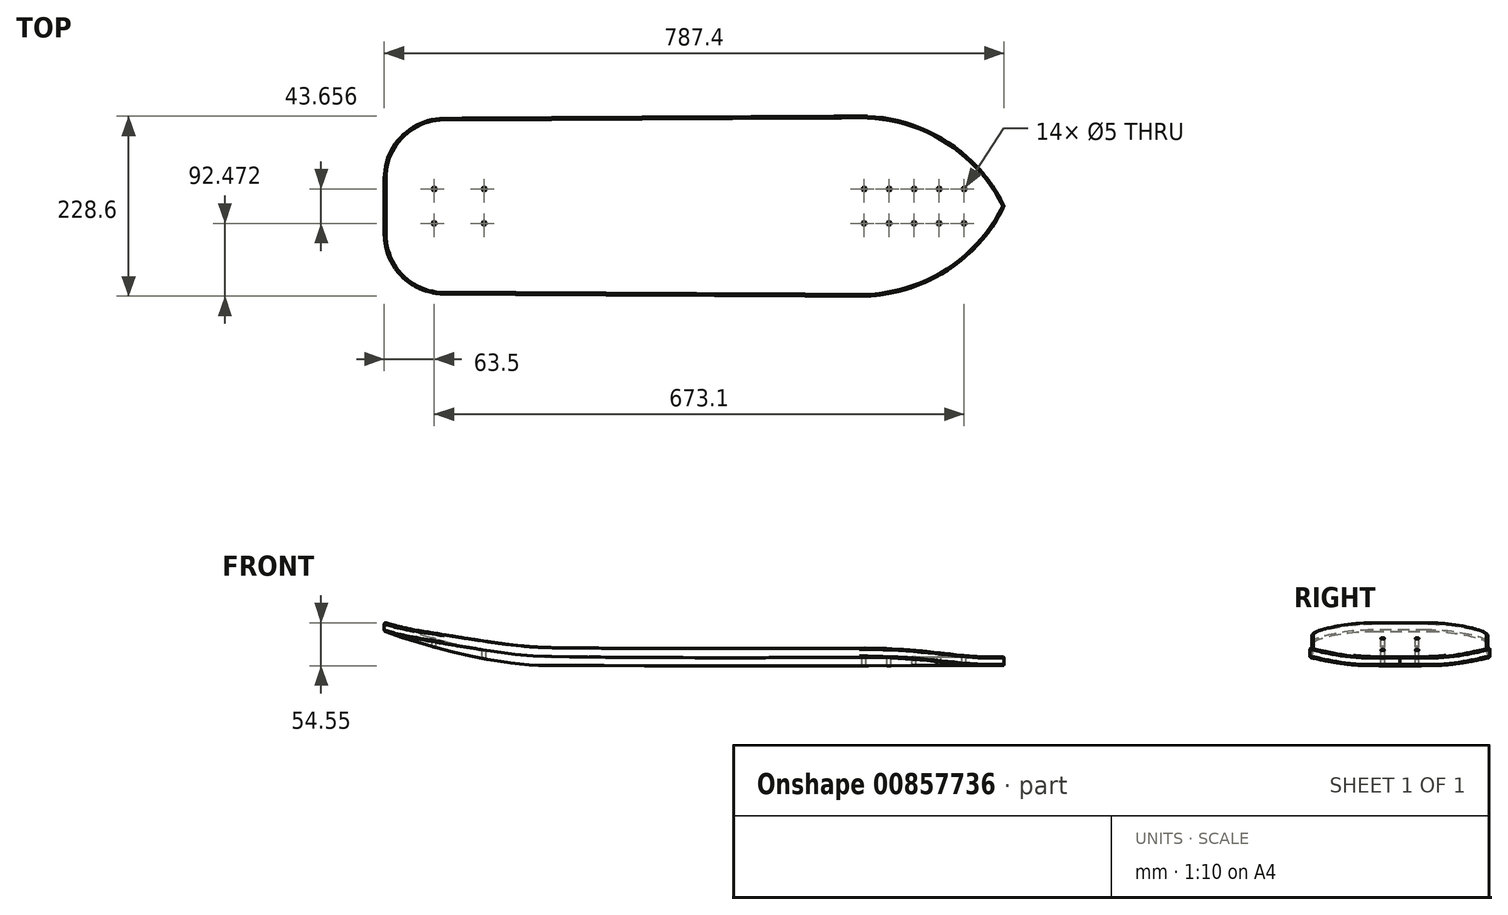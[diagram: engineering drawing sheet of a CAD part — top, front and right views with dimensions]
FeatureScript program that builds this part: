
annotation { "Feature Type Name" : "Feature", "Feature Type Description" : "" }
export const myFeature = defineFeature(function(context is Context, id is Id, definition is map)
    precondition{}
    {
        {
            var Q0;
            Q0=qCreatedBy(makeId("Front.planeOp"),FACE);
            var sketch = newSketch(context, id + "F0", { "sketchPlane" : qUnion([Q0])});
            skArc(sketch, "E0", {"start": v(-79.4, 6.95) * mm, "mid": v(-39.85, 1.74) * mm, "end": v(0, 0) * mm});
            skLineSegment(sketch, "E1", {"start": v(0, 0) * mm, "end": v(571.5, 0) * mm});
            skLineSegment(sketch, "E2", {"start": v(-79.4, 6.95) * mm, "end": v(-218.1, 31.4) * mm, "construction": true});
            skArc(sketch, "E3", {"start": v(-215.9, 43.91) * mm, "mid": v(-148.48, 22.36) * mm, "end": v(-79.4, 6.95) * mm});
            skLineSegment(sketch, "E4", {"start": v(-218.1, 31.4) * mm, "end": v(-215.9, 43.91) * mm, "construction": true});
            skPoint(sketch, "E5", {"position": v(-152.4, 0) * mm});
            skPoint(sketch, "E6", {"position": v(-88.9, 0) * mm});
            skPoint(sketch, "E7", {"position": v(393.7, 0) * mm});
            skPoint(sketch, "E8", {"position": v(520.7, 0) * mm});
            skPoint(sketch, "E9", {"position": v(488.95, 0) * mm});
            skPoint(sketch, "E10", {"position": v(425.45, 0) * mm});
            skPoint(sketch, "E11", {"position": v(457.2, 0) * mm});
            skSolve(sketch);
        }
        {
            var Q0;
            Q0=qCreatedBy(makeId("Top.planeOp"),FACE);
            var sketch = newSketch(context, id + "F1", { "sketchPlane" : qUnion([Q0])});
            skLineSegment(sketch, "E12", {"start": v(-140.1, 111.52) * mm, "end": v(387.71, 114.3) * mm});
            skLineSegment(sketch, "E13", {"start": v(387.71, -114.3) * mm, "end": v(-140.1, -111.52) * mm});
            skArc(sketch, "E14.filletArc", {"start": v(571.5, 0) * mm, "mid": v(496.09, 83.65) * mm, "end": v(387.71, 114.3) * mm});
            skArc(sketch, "E15.filletArc", {"start": v(387.71, -114.3) * mm, "mid": v(496.09, -83.65) * mm, "end": v(571.5, 0) * mm});
            skLineSegment(sketch, "E16", {"start": v(-215.9, 35.32) * mm, "end": v(-215.9, -35.32) * mm});
            skPoint(sketch, "E17.visualSharp", {"position": v(-215.9, 111.13) * mm});
            skArc(sketch, "E17.filletArc", {"start": v(-140.1, 111.52) * mm, "mid": v(-193.72, 89.06) * mm, "end": v(-215.9, 35.32) * mm});
            skPoint(sketch, "E18.visualSharp", {"position": v(-215.9, -111.12) * mm});
            skArc(sketch, "E18.filletArc", {"start": v(-215.9, -35.32) * mm, "mid": v(-193.72, -89.06) * mm, "end": v(-140.1, -111.52) * mm});
            skLineSegment(sketch, "E19", {"start": v(571.5, 0) * mm, "end": v(-215.9, 0) * mm, "construction": true});
            skPoint(sketch, "E20", {"position": v(388.78, -114.3) * mm});
            skPoint(sketch, "E21", {"position": v(388.78, 114.3) * mm});
            skLineSegment(sketch, "E22", {"start": v(388.78, 88.9) * mm, "end": v(388.78, 0) * mm, "construction": true});
            skLineSegment(sketch, "E23", {"start": v(388.78, 0) * mm, "end": v(388.78, -88.9) * mm, "construction": true});
            skLineSegment(sketch, "E24.0", {"start": v(-79.4, 0) * mm, "end": v(0, 0) * mm, "construction": true});
            skLineSegment(sketch, "E24.1", {"start": v(0, 0) * mm, "end": v(571.5, 0) * mm, "construction": true});
            skLineSegment(sketch, "E24.2", {"start": v(-79.4, 0) * mm, "end": v(-218.1, 0) * mm, "construction": true});
            skLineSegment(sketch, "E24.3", {"start": v(-215.9, 0) * mm, "end": v(-79.4, 0) * mm, "construction": true});
            skLineSegment(sketch, "E24.4", {"start": v(-218.1, 0) * mm, "end": v(-215.9, 0) * mm, "construction": true});
            skPoint(sketch, "E24.5", {"position": v(-152.4, 0) * mm});
            skPoint(sketch, "E24.6", {"position": v(-88.9, 0) * mm});
            skPoint(sketch, "E24.7", {"position": v(393.7, 0) * mm});
            skPoint(sketch, "E24.8", {"position": v(520.7, 0) * mm});
            skPoint(sketch, "E24.9", {"position": v(488.95, 0) * mm});
            skPoint(sketch, "E24.10", {"position": v(425.45, 0) * mm});
            skPoint(sketch, "E24.11", {"position": v(457.2, 0) * mm});
            skLineSegment(sketch, "E25", {"start": v(-152.4, 0) * mm, "end": v(-152.4, 21.83) * mm, "construction": true});
            skLineSegment(sketch, "E26", {"start": v(-152.4, 21.83) * mm, "end": v(-88.9, 21.83) * mm, "construction": true});
            skLineSegment(sketch, "E27", {"start": v(-88.9, 21.83) * mm, "end": v(-88.9, 0) * mm, "construction": true});
            skLineSegment(sketch, "E28", {"start": v(-88.9, 21.83) * mm, "end": v(520.7, 21.83) * mm, "construction": true});
            skLineSegment(sketch, "E29", {"start": v(520.7, 0) * mm, "end": v(520.7, 21.83) * mm, "construction": true});
            skLineSegment(sketch, "E30", {"start": v(488.95, 0) * mm, "end": v(488.95, 21.83) * mm, "construction": true});
            skLineSegment(sketch, "E31", {"start": v(457.2, 0) * mm, "end": v(457.2, 21.83) * mm, "construction": true});
            skLineSegment(sketch, "E32", {"start": v(425.45, 0) * mm, "end": v(425.45, 21.83) * mm, "construction": true});
            skLineSegment(sketch, "E33", {"start": v(393.7, 0) * mm, "end": v(393.7, 21.83) * mm, "construction": true});
            skCircle(sketch, "E34", {"center": v(-152.4, 21.83) * mm, "radius": 2.5 * mm});
            skCircle(sketch, "E35", {"center": v(-88.9, 21.83) * mm, "radius": 2.5 * mm});
            skCircle(sketch, "E36", {"center": v(393.7, 21.83) * mm, "radius": 2.5 * mm});
            skCircle(sketch, "E37", {"center": v(425.45, 21.83) * mm, "radius": 2.5 * mm});
            skCircle(sketch, "E38", {"center": v(457.2, 21.83) * mm, "radius": 2.5 * mm});
            skCircle(sketch, "E39", {"center": v(488.95, 21.83) * mm, "radius": 2.5 * mm});
            skCircle(sketch, "E40", {"center": v(520.7, 21.83) * mm, "radius": 2.5 * mm});
            skCircle(sketch, "E41.MirrorC", {"center": v(520.7, -21.83) * mm, "radius": 2.5 * mm});
            skCircle(sketch, "E42.MirrorC", {"center": v(488.95, -21.83) * mm, "radius": 2.5 * mm});
            skCircle(sketch, "E43.MirrorC", {"center": v(457.2, -21.83) * mm, "radius": 2.5 * mm});
            skCircle(sketch, "E44.MirrorC", {"center": v(425.45, -21.83) * mm, "radius": 2.5 * mm});
            skCircle(sketch, "E45.MirrorC", {"center": v(393.7, -21.83) * mm, "radius": 2.5 * mm});
            skCircle(sketch, "E46.MirrorC", {"center": v(-88.9, -21.83) * mm, "radius": 2.5 * mm});
            skCircle(sketch, "E47.MirrorC", {"center": v(-152.4, -21.83) * mm, "radius": 2.5 * mm});
            skSolve(sketch);
        }
        {
            var Q0;
            Q0=sQuery(id+"F0.wireOp",VERTEX,"E3.start");
            var Q1;
            Q1=sQuery(id+"F0.wireOp",EDGE,"E3");
            cPlane(context, id + "F2", {"entities" : qUnion([Q0, Q1]), "cplaneType" : CPlaneType.LINE_ANGLE, "offset" : 25.4 * mm, "angle" : 0 * degree, "width" : 152.4 * mm, "height" : 152.4 * mm});
        }
        {
            var Q0;
            Q0=sQuery(id+"F0.wireOp",VERTEX,"E0.start");
            var Q1;
            Q1=sQuery(id+"F0.wireOp",EDGE,"E0");
            cPlane(context, id + "F3", {"entities" : qUnion([Q0, Q1]), "cplaneType" : CPlaneType.LINE_ANGLE, "offset" : 25.4 * mm, "angle" : 0 * degree, "width" : 152.4 * mm, "height" : 152.4 * mm});
        }
        {
            var Q0;
            Q0=qCreatedBy(makeId("Origin.pointOp"),VERTEX);
            var Q1;
            Q1=sQuery(id+"F0.wireOp",EDGE,"E1");
            cPlane(context, id + "F4", {"entities" : qUnion([Q0, Q1]), "cplaneType" : CPlaneType.LINE_POINT, "offset" : 25.4 * mm, "width" : 152.4 * mm, "height" : 152.4 * mm});
        }
        {
            var Q0;
            Q0=sQuery(id+"F0.wireOp",VERTEX,"E1.end");
            var Q1;
            Q1=sQuery(id+"F0.wireOp",EDGE,"E1");
            cPlane(context, id + "F5", {"entities" : qUnion([Q0, Q1]), "cplaneType" : CPlaneType.LINE_POINT, "offset" : 25.4 * mm, "width" : 152.4 * mm, "height" : 152.4 * mm});
        }
        {
            var Q0;
            Q0=qCreatedBy(id+"F5.planeOp",FACE);
            var sketch = newSketch(context, id + "F6", { "sketchPlane" : qUnion([Q0])});
            skLineSegment(sketch, "E48", {"start": v(0, 0) * mm, "end": v(38.1, 0) * mm});
            skLineSegment(sketch, "E49", {"start": v(0, 0) * mm, "end": v(0, 134.88) * mm, "construction": true});
            skLineSegment(sketch, "E50.MirrorCS", {"start": v(0, 0) * mm, "end": v(-38.1, 0) * mm});
            skArc(sketch, "E51", {"start": v(38.1, 0) * mm, "mid": v(76.73, 3.2) * mm, "end": v(114.3, 12.7) * mm});
            skArc(sketch, "E52.MirrorCS", {"start": v(-38.1, 0) * mm, "mid": v(-76.73, 3.2) * mm, "end": v(-114.3, 12.7) * mm});
            skArc(sketch, "E53.0", {"start": v(-38.1, -11.11) * mm, "mid": v(-76.68, -8.07) * mm, "end": v(-114.3, 0.98) * mm});
            skLineSegment(sketch, "E53.1", {"start": v(0, -11.11) * mm, "end": v(-38.1, -11.11) * mm});
            skLineSegment(sketch, "E53.2", {"start": v(0, -11.11) * mm, "end": v(38.1, -11.11) * mm});
            skArc(sketch, "E53.3", {"start": v(38.1, -11.11) * mm, "mid": v(76.68, -8.07) * mm, "end": v(114.3, 0.98) * mm});
            skLineSegment(sketch, "E54", {"start": v(-114.3, 12.7) * mm, "end": v(-114.3, 0.98) * mm});
            skLineSegment(sketch, "E55", {"start": v(114.3, 12.7) * mm, "end": v(114.3, 0.98) * mm});
            skLineSegment(sketch, "E56", {"start": v(0, 0) * mm, "end": v(0, -11.11) * mm, "construction": true});
            skSolve(sketch);
        }
        {
            var Q0;
            Q0=qCreatedBy(id+"F4.planeOp",FACE);
            var sketch = newSketch(context, id + "F7", { "sketchPlane" : qUnion([Q0])});
            skLineSegment(sketch, "E57", {"start": v(0, 0) * mm, "end": v(0, 50.5) * mm, "construction": true});
            skLineSegment(sketch, "E58", {"start": v(0, 0) * mm, "end": v(0, -11.11) * mm, "construction": true});
            skLineSegment(sketch, "E59", {"start": v(0, 0) * mm, "end": v(25.4, 0) * mm});
            skArc(sketch, "E60", {"start": v(25.4, 0) * mm, "mid": v(70.3, 3.2) * mm, "end": v(114.3, 12.7) * mm});
            skLineSegment(sketch, "E61.MirrorCS", {"start": v(0, 0) * mm, "end": v(-25.4, 0) * mm});
            skArc(sketch, "E62.MirrorCS", {"start": v(-25.4, 0) * mm, "mid": v(-70.3, 3.2) * mm, "end": v(-114.3, 12.7) * mm});
            skArc(sketch, "E63.0", {"start": v(-25.4, -11.11) * mm, "mid": v(-70.27, -8.03) * mm, "end": v(-114.3, 1.14) * mm});
            skLineSegment(sketch, "E63.1", {"start": v(0, -11.11) * mm, "end": v(-25.4, -11.11) * mm});
            skLineSegment(sketch, "E63.2", {"start": v(0, -11.11) * mm, "end": v(25.4, -11.11) * mm});
            skArc(sketch, "E63.3", {"start": v(25.4, -11.11) * mm, "mid": v(70.27, -8.03) * mm, "end": v(114.3, 1.14) * mm});
            skLineSegment(sketch, "E64", {"start": v(114.3, 12.7) * mm, "end": v(114.3, 1.14) * mm});
            skLineSegment(sketch, "E65", {"start": v(-114.3, 12.7) * mm, "end": v(-114.3, 1.14) * mm});
            skSolve(sketch);
        }
        {
            var Q0;
            Q0=qCreatedBy(id+"F3.planeOp",FACE);
            var sketch = newSketch(context, id + "F8", { "sketchPlane" : qUnion([Q0])});
            skLineSegment(sketch, "E66", {"start": v(0, -6.95) * mm, "end": v(25.4, -6.95) * mm});
            skLineSegment(sketch, "E67", {"start": v(0, -6.95) * mm, "end": v(0, 35.44) * mm, "construction": true});
            skArc(sketch, "E68", {"start": v(25.4, -6.95) * mm, "mid": v(70.3, -3.75) * mm, "end": v(114.3, 5.75) * mm});
            skLineSegment(sketch, "E69", {"start": v(0, -6.95) * mm, "end": v(0, -17.89) * mm, "construction": true});
            skArc(sketch, "E70.MirrorCS", {"start": v(-25.4, -6.95) * mm, "mid": v(-70.3, -3.75) * mm, "end": v(-114.3, 5.75) * mm});
            skLineSegment(sketch, "E71.MirrorCS", {"start": v(0, -6.95) * mm, "end": v(-25.4, -6.95) * mm});
            skArc(sketch, "E72.0", {"start": v(-25.4, -17.89) * mm, "mid": v(-70.27, -14.81) * mm, "end": v(-114.3, -5.63) * mm});
            skLineSegment(sketch, "E72.1", {"start": v(0, -17.89) * mm, "end": v(-25.4, -17.89) * mm});
            skLineSegment(sketch, "E72.2", {"start": v(0, -17.89) * mm, "end": v(25.4, -17.89) * mm});
            skArc(sketch, "E72.3", {"start": v(25.4, -17.89) * mm, "mid": v(70.27, -14.81) * mm, "end": v(114.3, -5.63) * mm});
            skLineSegment(sketch, "E73", {"start": v(114.3, 5.75) * mm, "end": v(114.3, -5.63) * mm});
            skLineSegment(sketch, "E74", {"start": v(-114.3, 5.75) * mm, "end": v(-114.3, -5.63) * mm});
            skSolve(sketch);
        }
        {
            var Q0;
            Q0=qCreatedBy(id+"F2.planeOp",FACE);
            var sketch = newSketch(context, id + "F9", { "sketchPlane" : qUnion([Q0])});
            skLineSegment(sketch, "E75", {"start": v(0, -33.74) * mm, "end": v(12.7, -33.74) * mm});
            skLineSegment(sketch, "E76", {"start": v(12.7, -33.74) * mm, "end": v(114.3, -33.74) * mm});
            skLineSegment(sketch, "E77", {"start": v(114.3, -33.74) * mm, "end": v(114.3, -44.16) * mm});
            skLineSegment(sketch, "E78", {"start": v(114.3, -44.16) * mm, "end": v(12.7, -44.16) * mm});
            skLineSegment(sketch, "E79", {"start": v(12.7, -44.16) * mm, "end": v(0, -44.16) * mm});
            skLineSegment(sketch, "E80", {"start": v(0, -44.16) * mm, "end": v(-12.7, -44.16) * mm});
            skLineSegment(sketch, "E81", {"start": v(-12.7, -44.16) * mm, "end": v(-114.3, -44.16) * mm});
            skLineSegment(sketch, "E82", {"start": v(-114.3, -44.16) * mm, "end": v(-114.3, -33.74) * mm});
            skLineSegment(sketch, "E83", {"start": v(-114.3, -33.74) * mm, "end": v(-12.7, -33.74) * mm});
            skLineSegment(sketch, "E84", {"start": v(-12.7, -33.74) * mm, "end": v(0, -33.74) * mm});
            skLineSegment(sketch, "E85", {"start": v(0, -33.74) * mm, "end": v(0, -44.16) * mm, "construction": true});
            skSolve(sketch);
        }
        {
            var Q0;
            Q0 = qConstructionFilter(qBodyType(qCreatedBy(id + "F0" ,EDGE), BodyType.WIRE), ConstructionObject.NO);
            var Q1;
            Q1=makeQuery(id+"F6.imprint","IMPRINT",FACE,{"disambiguationData":[TD([[makeQuery(id+"F6.imprint","IMPRINT",EDGE,{"derivedFrom":sQuery(id+"F6.wireOp",EDGE,"E48")}),-1.0]])]});
            var Q2;
            Q2=makeQuery(id+"F7.imprint","IMPRINT",FACE,{"disambiguationData":[TD([[makeQuery(id+"F7.imprint","IMPRINT",EDGE,{"derivedFrom":sQuery(id+"F7.wireOp",EDGE,"E59")}),-1.0]])]});
            var Q3;
            Q3=makeQuery(id+"F8.imprint","IMPRINT",FACE,{"disambiguationData":[TD([[makeQuery(id+"F8.imprint","IMPRINT",EDGE,{"derivedFrom":sQuery(id+"F8.wireOp",EDGE,"E66")}),-1.0]])]});
            var Q4;
            Q4=makeQuery(id+"F9.imprint","IMPRINT",FACE,{"disambiguationData":[TD([[makeQuery(id+"F9.imprint","IMPRINT",EDGE,{"derivedFrom":sQuery(id+"F9.wireOp",EDGE,"E75")}),-1.0]])]});
            loft(context, id + "F10", {"addSections" : true, "spine" : qUnion([Q0]), "sectionCount" : 31, "sheetProfilesArray" : [{ "sheetProfileEntities" : qUnion([Q1]) }, { "sheetProfileEntities" : qUnion([Q2]) }, { "sheetProfileEntities" : qUnion([Q3]) }, { "sheetProfileEntities" : qUnion([Q4]) }]});
        }
        {
            var Q0;
            Q0 = qSketchRegion(id + "F1", true);
            extrude(context, id + "F11", {"entities" : qUnion([Q0]), "endBound" : BoundingType.THROUGH_ALL, "oppositeDirection" : true, "depth" : 25.4 * mm, "offsetDistance" : 25.4 * mm, "hasSecondDirection" : true, "secondDirectionBound" : SecondDirectionBoundingType.THROUGH_ALL, "secondDirectionOppositeDirection" : false, "secondDirectionDepth" : 25.4 * mm});
        }
        {
            var Q0;
            Q0=makeQuery(id+"F11.opExtrude","SWEPT_BODY",BODY,{"disambiguationData":[OSD([sQuery(id+"F1.wireOp",EDGE,"E12"),sQuery(id+"F1.wireOp",EDGE,"E13"),sQuery(id+"F1.wireOp",EDGE,"E14.filletArc"),sQuery(id+"F1.wireOp",EDGE,"E15.filletArc"),sQuery(id+"F1.wireOp",EDGE,"E16"),sQuery(id+"F1.wireOp",EDGE,"E17.filletArc"),sQuery(id+"F1.wireOp",EDGE,"E18.filletArc"),sQuery(id+"F1.wireOp",EDGE,"E34"),sQuery(id+"F1.wireOp",EDGE,"E35"),sQuery(id+"F1.wireOp",EDGE,"E36"),sQuery(id+"F1.wireOp",EDGE,"E37"),sQuery(id+"F1.wireOp",EDGE,"E38"),sQuery(id+"F1.wireOp",EDGE,"E39"),sQuery(id+"F1.wireOp",EDGE,"E40"),sQuery(id+"F1.wireOp",EDGE,"E41.MirrorC"),sQuery(id+"F1.wireOp",EDGE,"E42.MirrorC"),sQuery(id+"F1.wireOp",EDGE,"E43.MirrorC"),sQuery(id+"F1.wireOp",EDGE,"E44.MirrorC"),sQuery(id+"F1.wireOp",EDGE,"E45.MirrorC"),sQuery(id+"F1.wireOp",EDGE,"E46.MirrorC"),sQuery(id+"F1.wireOp",EDGE,"E47.MirrorC")])]});
            var Q1;
            Q1=makeQuery(id+"F10.opLoft","SWEPT_BODY",BODY,{"disambiguationData":[OSD([makeQuery(id+"F6.imprint","IMPRINT",FACE,{"disambiguationData":[TD([[makeQuery(id+"F6.imprint","IMPRINT",EDGE,{"derivedFrom":sQuery(id+"F6.wireOp",EDGE,"E48")}),-1.0]])]}),sQuery(id+"F7.wireOp",EDGE,"E63.2"),sQuery(id+"F8.wireOp",EDGE,"E72.1"),makeQuery(id+"F9.imprint","IMPRINT",FACE,{"disambiguationData":[TD([[makeQuery(id+"F9.imprint","IMPRINT",EDGE,{"derivedFrom":sQuery(id+"F9.wireOp",EDGE,"E75")}),-1.0]])]})])]});
            booleanBodies(context, id + "F12", {"operationType" : BooleanOperationType.INTERSECTION, "tools" : qUnion([Q0, Q1])});
        }
        {
            var Q0;
            Q0=makeQuery(id+"F12.opBoolean","INTERSECT",EDGE,{"derivedFrom":[makeQuery(id+"F10.opLoft","SWEPT_FACE",FACE,{"disambiguationData":[OSD([sQuery(id+"F6.wireOp",EDGE,"E50.MirrorCS"),sQuery(id+"F6.wireOp",EDGE,"E52.MirrorCS"),sQuery(id+"F6.wireOp",EDGE,"E54"),sQuery(id+"F7.wireOp",EDGE,"E61.MirrorCS"),sQuery(id+"F7.wireOp",EDGE,"E62.MirrorCS"),sQuery(id+"F7.wireOp",EDGE,"E65"),sQuery(id+"F8.wireOp",EDGE,"E70.MirrorCS"),sQuery(id+"F8.wireOp",EDGE,"E71.MirrorCS"),sQuery(id+"F8.wireOp",EDGE,"E74"),sQuery(id+"F9.wireOp",EDGE,"E82"),sQuery(id+"F9.wireOp",EDGE,"E83"),sQuery(id+"F9.wireOp",EDGE,"E84")])]}),makeQuery(id+"F11.opExtrude","SWEPT_FACE",FACE,{"disambiguationData":[OSD([sQuery(id+"F1.wireOp",EDGE,"E13")])]})]});
            var Q1;
            Q1=makeQuery(id+"F12.opBoolean","INTERSECT",EDGE,{"derivedFrom":[makeQuery(id+"F10.opLoft","SWEPT_FACE",FACE,{"disambiguationData":[OSD([sQuery(id+"F6.wireOp",EDGE,"E53.2"),sQuery(id+"F6.wireOp",EDGE,"E53.3"),sQuery(id+"F6.wireOp",EDGE,"E55"),sQuery(id+"F7.wireOp",EDGE,"E63.2"),sQuery(id+"F7.wireOp",EDGE,"E63.3"),sQuery(id+"F7.wireOp",EDGE,"E64"),sQuery(id+"F8.wireOp",EDGE,"E72.2"),sQuery(id+"F8.wireOp",EDGE,"E72.3"),sQuery(id+"F8.wireOp",EDGE,"E73"),sQuery(id+"F9.wireOp",EDGE,"E77"),sQuery(id+"F9.wireOp",EDGE,"E78"),sQuery(id+"F9.wireOp",EDGE,"E79")])]}),makeQuery(id+"F11.opExtrude","SWEPT_FACE",FACE,{"disambiguationData":[OSD([sQuery(id+"F1.wireOp",EDGE,"E13")])]})]});
            fillet(context, id + "F13", {"entities" : qUnion([Q0, Q1]), "radius" : 1.59 * mm, "tangentPropagation" : true, "allowEdgeOverflow" : false});
        }
    });
